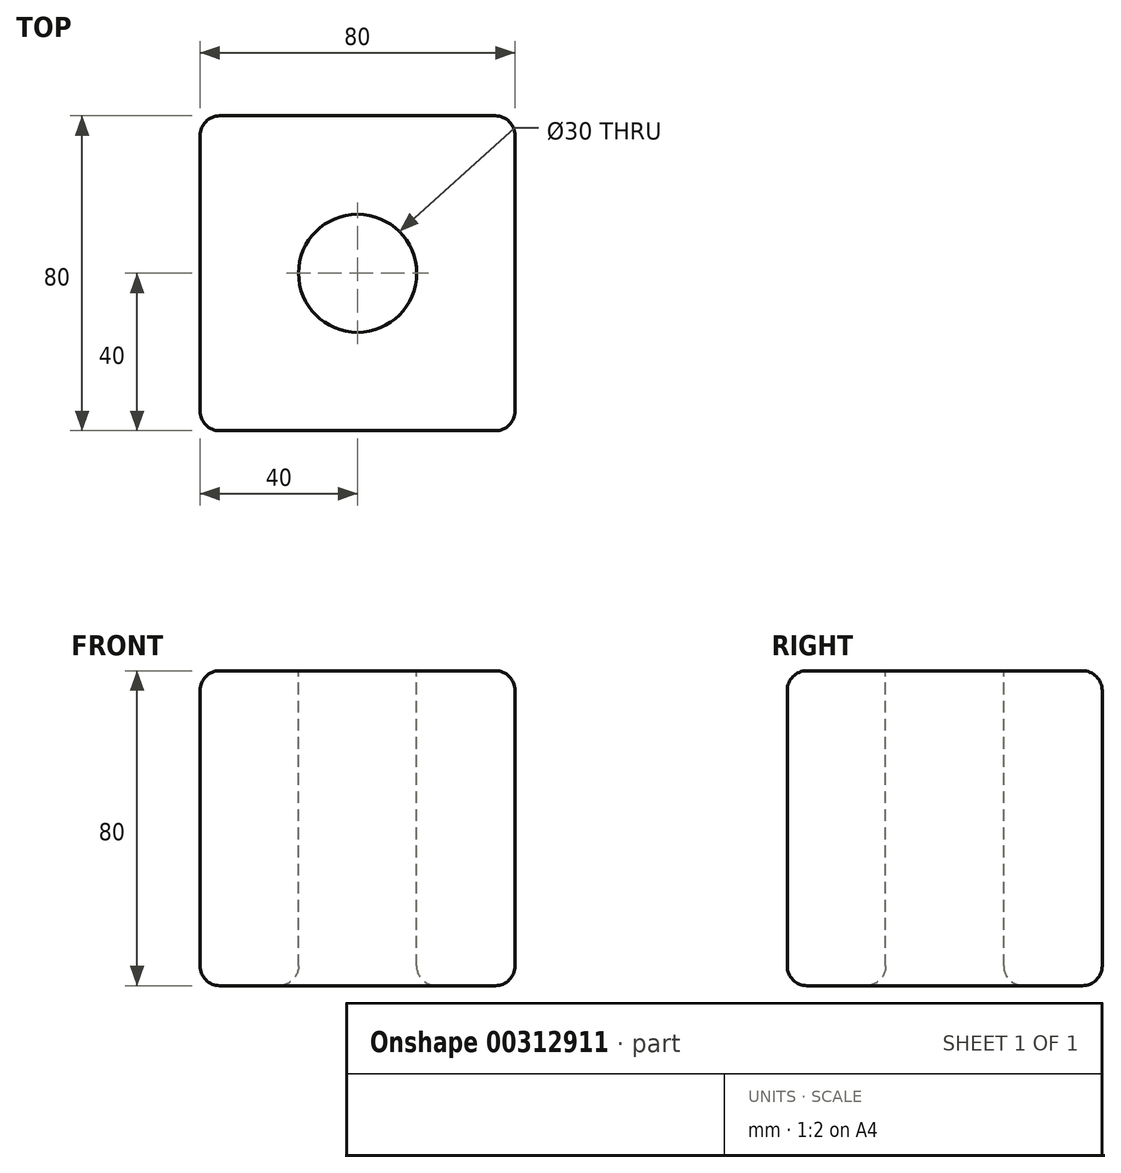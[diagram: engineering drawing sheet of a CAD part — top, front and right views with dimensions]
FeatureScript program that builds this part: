
annotation { "Feature Type Name" : "Feature", "Feature Type Description" : "" }
export const myFeature = defineFeature(function(context is Context, id is Id, definition is map)
    precondition{}
    {
        {
            var Q0;
            Q0=qCreatedBy(makeId("Top.planeOp"),FACE);
            var sketch = newSketch(context, id + "F0", { "sketchPlane" : qUnion([Q0])});
            skLineSegment(sketch, "E0.bottom", {"start": v(40, 40) * mm, "end": v(-40, 40) * mm});
            skLineSegment(sketch, "E0.top", {"start": v(40, -40) * mm, "end": v(-40, -40) * mm});
            skLineSegment(sketch, "E0.left", {"start": v(40, 40) * mm, "end": v(40, -40) * mm});
            skLineSegment(sketch, "E0.right", {"start": v(-40, 40) * mm, "end": v(-40, -40) * mm});
            skPoint(sketch, "E0.middle", {"position": v(0, 0) * mm});
            skSolve(sketch);
        }
        {
            var Q0;
            Q0=makeQuery(id+"F0.imprint","IMPRINT",FACE,{"disambiguationData":[TD([[makeQuery(id+"F0.imprint","IMPRINT",EDGE,{"derivedFrom":sQuery(id+"F0.wireOp",EDGE,"E0.bottom")}),1.0]])]});
            extrude(context, id + "F1", {"entities" : qUnion([Q0]), "endBound" : BoundingType.SYMMETRIC, "depth" : 80 * mm});
        }
        {
            var Q0;
            Q0=makeQuery(id+"F1.opExtrude","CAP_EDGE",EDGE,{"disambiguationData":[OSD([sQuery(id+"F0.wireOp",EDGE,"E0.right")])],"isStart":false});
            var Q1;
            Q1=makeQuery(id+"F1.opExtrude","CAP_EDGE",EDGE,{"disambiguationData":[OSD([sQuery(id+"F0.wireOp",EDGE,"E0.bottom")])],"isStart":false});
            var Q2;
            Q2=makeQuery(id+"F1.opExtrude","CAP_EDGE",EDGE,{"disambiguationData":[OSD([sQuery(id+"F0.wireOp",EDGE,"E0.left")])],"isStart":false});
            var Q3;
            Q3=makeQuery(id+"F1.opExtrude","CAP_EDGE",EDGE,{"disambiguationData":[OSD([sQuery(id+"F0.wireOp",EDGE,"E0.top")])],"isStart":false});
            var Q4;
            Q4=makeQuery(id+"F1.opExtrude","SWEPT_EDGE",EDGE,{"disambiguationData":[OSD([sQuery(id+"F0.wireOp",EDGE,"E0.bottom"),sQuery(id+"F0.wireOp",EDGE,"E0.left")])]});
            var Q5;
            Q5=makeQuery(id+"F1.opExtrude","SWEPT_EDGE",EDGE,{"disambiguationData":[OSD([sQuery(id+"F0.wireOp",EDGE,"E0.top"),sQuery(id+"F0.wireOp",EDGE,"E0.left")])]});
            var Q6;
            Q6=makeQuery(id+"F1.opExtrude","CAP_EDGE",EDGE,{"disambiguationData":[OSD([sQuery(id+"F0.wireOp",EDGE,"E0.left")])],"isStart":true});
            var Q7;
            Q7=makeQuery(id+"F1.opExtrude","CAP_FACE",FACE,{"disambiguationData":[OSD([sQuery(id+"F0.wireOp",EDGE,"E0.bottom"),sQuery(id+"F0.wireOp",EDGE,"E0.top"),sQuery(id+"F0.wireOp",EDGE,"E0.left"),sQuery(id+"F0.wireOp",EDGE,"E0.right")])],"isStart":false});
            var Q8;
            Q8=makeQuery(id+"F1.opExtrude","SWEPT_EDGE",EDGE,{"disambiguationData":[OSD([sQuery(id+"F0.wireOp",EDGE,"E0.bottom"),sQuery(id+"F0.wireOp",EDGE,"E0.right")])]});
            var Q9;
            Q9=makeQuery(id+"F1.opExtrude","CAP_EDGE",EDGE,{"disambiguationData":[OSD([sQuery(id+"F0.wireOp",EDGE,"E0.bottom")])],"isStart":true});
            var Q10;
            Q10=makeQuery(id+"F1.opExtrude","CAP_EDGE",EDGE,{"disambiguationData":[OSD([sQuery(id+"F0.wireOp",EDGE,"E0.top")])],"isStart":true});
            var Q11;
            Q11=makeQuery(id+"F1.opExtrude","SWEPT_EDGE",EDGE,{"disambiguationData":[OSD([sQuery(id+"F0.wireOp",EDGE,"E0.top"),sQuery(id+"F0.wireOp",EDGE,"E0.right")])]});
            var Q12;
            Q12=makeQuery(id+"F1.opExtrude","CAP_EDGE",EDGE,{"disambiguationData":[OSD([sQuery(id+"F0.wireOp",EDGE,"E0.right")])],"isStart":true});
            fillet(context, id + "F2", {"entities" : qUnion([Q0, Q1, Q2, Q3, Q4, Q5, Q6, Q7, Q8, Q9, Q10, Q11, Q12]), "radius" : 5 * mm, "tangentPropagation" : true, "allowEdgeOverflow" : false});
        }
        {
            var Q0;
            Q0=makeQuery(id+"F1.opExtrude","CAP_FACE",FACE,{"disambiguationData":[OSD([sQuery(id+"F0.wireOp",EDGE,"E0.bottom"),sQuery(id+"F0.wireOp",EDGE,"E0.top"),sQuery(id+"F0.wireOp",EDGE,"E0.left"),sQuery(id+"F0.wireOp",EDGE,"E0.right")])],"isStart":false});
            var sketch = newSketch(context, id + "F3", { "sketchPlane" : qUnion([Q0])});
            skCircle(sketch, "E1", {"center": v(0, 0) * mm, "radius": 15 * mm});
            skSolve(sketch);
        }
        {
            var Q0;
            Q0=makeQuery(id+"F3.imprint","IMPRINT",FACE,{"disambiguationData":[TD([[makeQuery(id+"F3.imprint","IMPRINT",EDGE,{"derivedFrom":sQuery(id+"F3.wireOp",EDGE,"E1")}),1.0]])]});
            extrude(context, id + "F4", {"entities" : qUnion([Q0]), "operationType" : NewBodyOperationType.REMOVE, "endBound" : BoundingType.THROUGH_ALL, "oppositeDirection" : true, "depth" : 25 * mm});
        }
        {
            var Q0;
            Q0=makeQuery(id+"F4.boolean.opBoolean","INTERSECT",EDGE,{"derivedFrom":[makeQuery(id+"F1.opExtrude","CAP_FACE",FACE,{"disambiguationData":[OSD([sQuery(id+"F0.wireOp",EDGE,"E0.bottom"),sQuery(id+"F0.wireOp",EDGE,"E0.top"),sQuery(id+"F0.wireOp",EDGE,"E0.left"),sQuery(id+"F0.wireOp",EDGE,"E0.right")])],"isStart":true}),makeQuery(id+"F4.opExtrude","SWEPT_FACE",FACE,{"disambiguationData":[OSD([sQuery(id+"F3.wireOp",EDGE,"E1")])]})]});
            var Q1;
            Q1=makeQuery(id+"F4.boolean.opBoolean","COPY",EDGE,{"derivedFrom":makeQuery(id+"F4.opExtrude","CAP_EDGE",EDGE,{"disambiguationData":[OSD([sQuery(id+"F3.wireOp",EDGE,"E1")])],"isStart":true})});
            fillet(context, id + "F5", {"entities" : qUnion([Q0, Q1]), "radius" : 5 * mm, "tangentPropagation" : true, "allowEdgeOverflow" : false});
        }
    });
